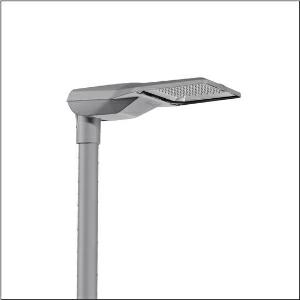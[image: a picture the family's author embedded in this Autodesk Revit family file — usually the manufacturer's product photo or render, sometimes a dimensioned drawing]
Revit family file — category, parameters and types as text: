
# Revit family: streetlight_sl_21_iq_midi___stw1_0a_5xe3e21d08nb_941d
name_source: partatom
category: Lighting Fixtures
units: mm (PartAtom-declared; Revit-internal decimal feet)

## family parameters
Cut with Voids When Loaded = No
Host = Face
Light Source = No
Part Type = Normal
Room Calculation Point = No
Round Connector Dimension = Use Diameter
Shared = No

## types (1)
- --- (1 x LED, 19210 lm, 155.5 W, 2200K)
    Apparent Load = 155 VA
    CIE Flux Codes = 39 75 98 100 100
    Color Rendering = 70
    Color Temperature = 2200K
    Default Elevation = 1800 mm
    Description = Streetlight SL 21 iQ midi, mast luminaire, primary light control with lens, of PMMA, primary optical cover: cover, of toughened safety glass, transparent, light distribution: STW1.0a, light emission: direct distribution, primary light characteristic: asymmetric, installation type: post-top, side-entry, LED, High Power LED, rated luminous flux: 19.210lm, luminous efficacy: 124lm/W, light colour: 722, colour temperature: 2200K, control: Auto-Match, Temp-Guard, Lumen-Switch, Night-Set, Smart-Wire, Light-Fading, Desk-Remote (wireless, voltage-free reading and setting of iQ features in the workshop via application-optimized NFC function/RFID function), optimised constant luminous flux control (CLO 2.0), presetting dimming linear, mains connection: 230..240V, AC, 50/60Hz, start of lifetime: 156W, end of service life: 162W, reduction: 69W, luminaire housing, of diecast aluminium, powder-coated, Siteco® metallic grey (DB 702S), corrosivity category C5 mid according to DIN EN ISO 12944, please order mast flange separately, inclination adjustable: 0°, 5°, 10°, 15°, sealing non-destructively replaceable, multi-level sealing system, length: 644mm, width: 335mm, height: 110mm, mast flange for spigot size: 42mm (side-entry): 5XC10008XM4, 60/48mm (side-entry/post-top): 5XC10108XM2, 76/60mm (side-entry/post-top): 5XC10108XM1, protection rating (complete): IP66, insulation class (complete): insulation class II (safety insulation), certification: CE, ENEC, ENEC+, VDE, impact resistance: IK09, permissible operating ambient temperature for outdoor applications: -40..+50°C, standard-compliant lighting for roads and squares, packaging unit: 1 piece

Light Distribution: STW1.0a
    Height = 111 mm
    Lamp = 1 x LED
    Lamp Light Flux = 19210 lm
    Lamp Power = 155.5 W
    Lamp count = 1
    Length = 644 mm
    Luminous efficacy = 124 lm/W
    Manufacturer = Siteco
    ModVariant = No
    Model = 5XE3E21D08NB
    Number of Poles = 1
    OnlyDefault = Yes
    Power Factor = 1
    Product Name = Streetlight SL 21 iQ midi | STW1.0a
    Product group = mast luminaire | pylon top
    ProductGroupID = 6100
    Protection Class = Protection class II
    Protection Degree = IP 66
    RLX_Detail_Level = 1
    RLX_Emergency_Light_Flux = 0 lm
    RLX_Emergency_Type = 0
    RLX_Emergency_Type_DB = No
    RlxData = <blob elided: 91237 chars, md5=497206e7>
    Socket = socket
    Standby Power = 0 W
    System Light Flux = 19210 lm
    System Power = 155 W
    Type Comments = factory setting: luminous flux: 100 % | dim-lin: 254 | 823 mA
    Type Image = l_1004298.jpg
    URL = http://relux.com
    VarID = @adj_120437
    Voltage = 0 V
    Weight = 0.00 kg
    Width = 336 mm

## geometry (parser evidence)
native form markers: Blend x4, Sweep x10
no freeform markers — native parametric forms only
